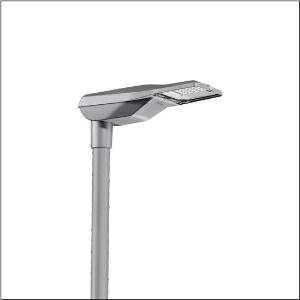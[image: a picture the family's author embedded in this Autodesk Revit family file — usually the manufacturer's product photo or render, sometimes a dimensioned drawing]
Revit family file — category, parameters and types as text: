
# Revit family: streetlight_sl_21_iq_micro___st1_0a_5xe1d41g08cb_d625
name_source: partatom
category: Lighting Fixtures
units: mm (PartAtom-declared; Revit-internal decimal feet)

## family parameters
Cut with Voids When Loaded = No
Host = Face
Light Source = No
Part Type = Normal
Room Calculation Point = No
Round Connector Dimension = Use Diameter
Shared = No

## types (1)
- --- (1 x LED, 2980 lm, 19.4 W, 4000K)
    Apparent Load = 19 VA
    CIE Flux Codes = 37 72 97 100 100
    Color Rendering = 70
    Color Temperature = 4000K
    Default Elevation = 1800 mm
    Description = Streetlight SL 21 iQ micro, mast luminaire, primary light control with lens, of PMMA, primary optical cover: cover, of toughened safety glass, transparent, light distribution: ST1.0a, light emission: direct distribution, primary light characteristic: asymmetric, installation type: post-top, side-entry, LED, High Power LED, rated luminous flux: 2.980lm, luminous efficacy: 154lm/W, light colour: 740, colour temperature: 4000K, control: Street-Remote, Auto-Match, Temp-Guard, Lumen-Switch, Night-Set, Smart-Wire, Light-Fading, Desk-Remote (wireless, voltage-free reading and setting of iQ features in the workshop via application-optimized NFC function/RFID function), optimised constant luminous flux control (CLO 2.0), presetting dimming linear, mains connection: 220..240V, AC, 50/60Hz, start of lifetime: 19W, end of service life: 20W, reduction: 10W, luminaire housing, of diecast aluminium, powder-coated, Siteco® metallic grey (DB 702S), corrosivity category C5 mid according to DIN EN ISO 12944, please order mast flange separately, inclination adjustable: 0°, 5°, 10°, 15°, sealing non-destructively replaceable, multi-level sealing system, length: 528mm, width: 235mm, height: 110mm, mast flange for spigot size: 42mm (side-entry): 5XC10008XM4, 60/48mm (side-entry/post-top): 5XC10108XM2, 76/60mm (side-entry/post-top): 5XC10108XM1, protection rating (complete): IP66, insulation class (complete): insulation class II (safety insulation), certification: CE, ENEC, ENEC+, VDE, impact resistance: IK09, permissible operating ambient temperature for outdoor applications: -40..+50°C, standard-compliant lighting for roads and squares, packaging unit: 1 piece

Light Distribution: ST1.0a
    Height = 110 mm
    Lamp = 1 x LED
    Lamp Light Flux = 2980 lm
    Lamp Power = 19.4 W
    Lamp count = 1
    Length = 528 mm
    Luminous efficacy = 154 lm/W
    Manufacturer = Siteco
    ModVariant = No
    Model = 5XE1D41G08CB
    Number of Poles = 1
    OnlyDefault = Yes
    Power Factor = 1
    Product Name = Streetlight SL 21 iQ micro | ST1.0a
    Product group = mast luminaire | pylon top
    ProductGroupID = 6100
    Protection Class = Protection class II
    Protection Degree = IP 66
    RLX_Detail_Level = 1
    RLX_Emergency_Light_Flux = 0 lm
    RLX_Emergency_Type = 0
    RLX_Emergency_Type_DB = No
    RlxData = <blob elided: 98557 chars, md5=d4c3d273>
    Socket = socket
    Standby Power = 0 W
    System Light Flux = 2980 lm
    System Power = 19 W
    Type Comments = factory setting: luminous flux: 100 % | dim-lin: 254 | 387 mA
    Type Image = l_1006881.jpg
    URL = http://relux.com
    VarID = @adj_070505
    Voltage = 0 V
    Weight = 0.00 kg
    Width = 235 mm

## geometry (parser evidence)
native form markers: Blend x4, Sweep x12
no freeform markers — native parametric forms only
